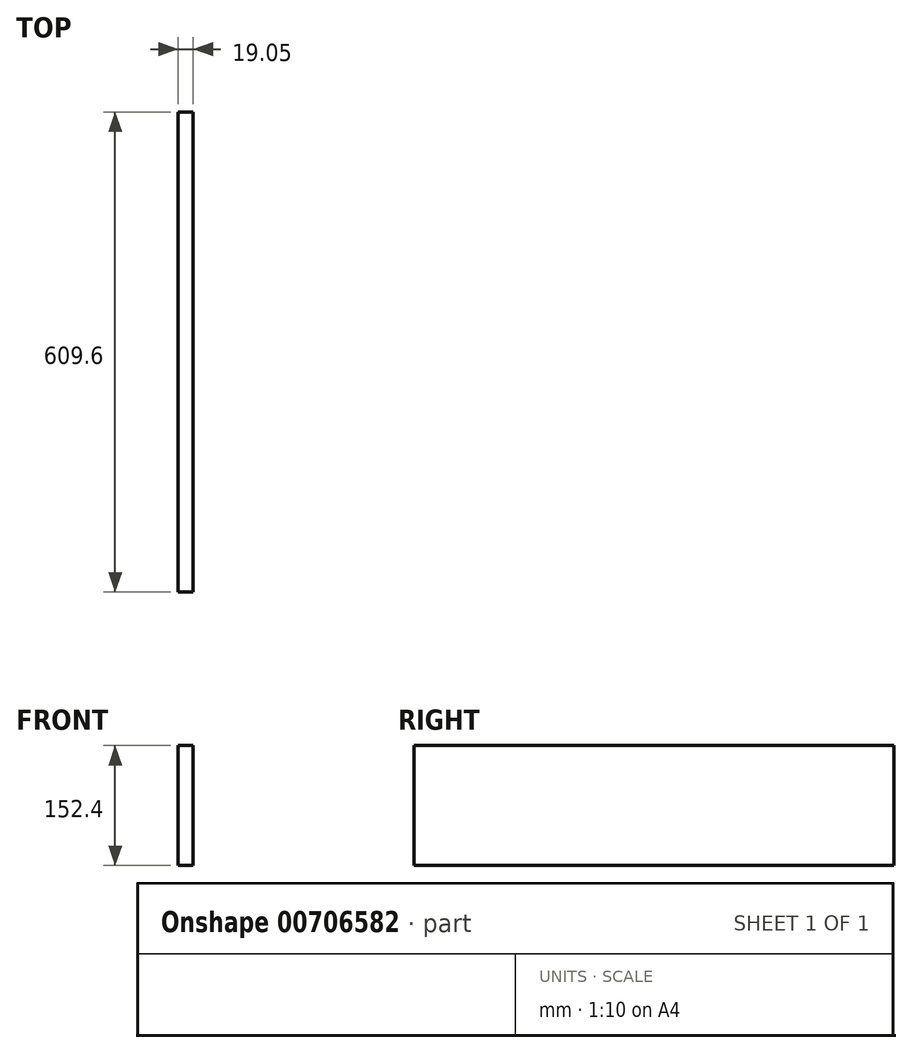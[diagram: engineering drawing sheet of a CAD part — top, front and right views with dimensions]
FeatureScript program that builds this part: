
annotation { "Feature Type Name" : "Feature", "Feature Type Description" : "" }
export const myFeature = defineFeature(function(context is Context, id is Id, definition is map)
    precondition{}
    {
        {
            var Q0;
            Q0=qCreatedBy(makeId("Right.planeOp"),FACE);
            var sketch = newSketch(context, id + "F0", { "sketchPlane" : qUnion([Q0])});
            skLineSegment(sketch, "E0.bottom", {"start": v(-304.8, 76.2) * mm, "end": v(304.8, 76.2) * mm});
            skLineSegment(sketch, "E0.top", {"start": v(-304.8, -76.2) * mm, "end": v(304.8, -76.2) * mm});
            skLineSegment(sketch, "E0.left", {"start": v(-304.8, 76.2) * mm, "end": v(-304.8, -76.2) * mm});
            skLineSegment(sketch, "E0.right", {"start": v(304.8, 76.2) * mm, "end": v(304.8, -76.2) * mm});
            skPoint(sketch, "E0.middle", {"position": v(0, 0) * mm});
            skSolve(sketch);
        }
        {
            var Q0;
            Q0=makeQuery(id+"F0.imprint","IMPRINT",FACE,{"disambiguationData":[TD([[makeQuery(id+"F0.imprint","IMPRINT",EDGE,{"derivedFrom":sQuery(id+"F0.wireOp",EDGE,"E0.bottom")}),-1.0]])]});
            extrude(context, id + "F1", {"entities" : qUnion([Q0]), "depth" : 19.05 * mm, "offsetDistance" : 25.4 * mm});
        }
    });
